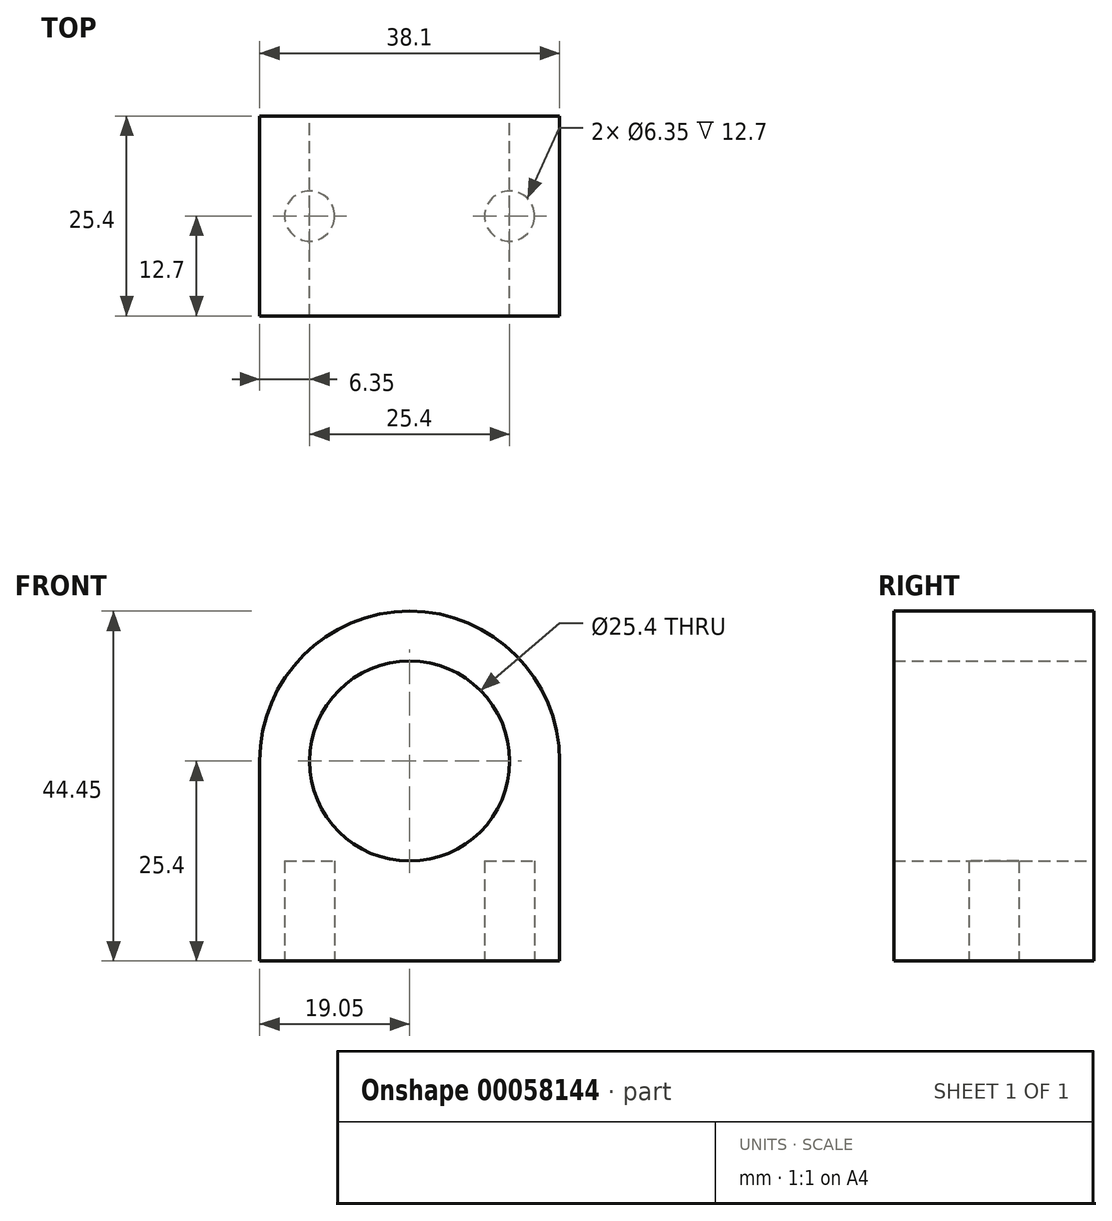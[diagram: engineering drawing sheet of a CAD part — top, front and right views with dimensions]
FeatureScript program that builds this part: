
annotation { "Feature Type Name" : "Feature", "Feature Type Description" : "" }
export const myFeature = defineFeature(function(context is Context, id is Id, definition is map)
    precondition{}
    {
        {
            var Q0;
            Q0=qCreatedBy(makeId("Front.planeOp"),FACE);
            var sketch = newSketch(context, id + "F0", { "sketchPlane" : qUnion([Q0])});
            skCircle(sketch, "E0", {"center": v(0, 0) * mm, "radius": 12.7 * mm});
            skArc(sketch, "E1", {"start": v(19.05, 0) * mm, "mid": v(0, 19.05) * mm, "end": v(-19.05, 0) * mm});
            skLineSegment(sketch, "E2", {"start": v(-19.05, 0) * mm, "end": v(-19.05, -25.4) * mm});
            skLineSegment(sketch, "E3", {"start": v(-19.05, -25.4) * mm, "end": v(19.05, -25.4) * mm});
            skLineSegment(sketch, "E4", {"start": v(19.05, -25.4) * mm, "end": v(19.05, 0) * mm});
            skSolve(sketch);
        }
        {
            var Q0;
            Q0 = qSketchRegion(id + "F0", true);
            extrude(context, id + "F1", {"entities" : qUnion([Q0]), "depth" : 25.4 * mm});
        }
        {
            var Q0;
            Q0=makeQuery(id+"F1.opExtrude","SWEPT_FACE",FACE,{"disambiguationData":[OSD([sQuery(id+"F0.wireOp",EDGE,"E3")])]});
            var sketch = newSketch(context, id + "F2", { "sketchPlane" : qUnion([Q0])});
            skCircle(sketch, "E5", {"center": v(12.7, 12.7) * mm, "radius": 3.18 * mm});
            skCircle(sketch, "E6", {"center": v(-12.7, 12.7) * mm, "radius": 3.18 * mm});
            skSolve(sketch);
        }
        {
            var Q0;
            Q0=makeQuery(id+"F2.imprint","IMPRINT",FACE,{"disambiguationData":[TD([[makeQuery(id+"F2.imprint","IMPRINT",EDGE,{"derivedFrom":sQuery(id+"F2.wireOp",EDGE,"E5")}),1.0]])]});
            var Q1;
            Q1=makeQuery(id+"F2.imprint","IMPRINT",FACE,{"disambiguationData":[TD([[makeQuery(id+"F2.imprint","IMPRINT",EDGE,{"derivedFrom":sQuery(id+"F2.wireOp",EDGE,"E6")}),1.0]])]});
            extrude(context, id + "F3", {"entities" : qUnion([Q0, Q1]), "operationType" : NewBodyOperationType.REMOVE, "oppositeDirection" : true, "depth" : 12.7 * mm});
        }
    });
